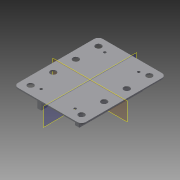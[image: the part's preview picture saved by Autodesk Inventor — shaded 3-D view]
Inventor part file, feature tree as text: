
AUTODESK INVENTOR PART (.ipt)
format: ipt  version: 2015 (Build 190159000, 159)  size: 258,048 bytes
history: native  units: mm
features: sketch x9, extrude x6, mirror x3, pattern_linear x3, fillet x2, plane x2, rib x2, hole x1
ambient origin geometry x8: Origin, YZ Plane, XZ Plane, XY Plane, X Axis, Y Axis, Z Axis, Center Point
bodies: Solid1 (feature_tree)
feature tree (28):
  extrude  "Extrusion1"  Depth=1.5mm
  fillet  "Fillet1"  Radius=1.5mm
  extrude  "Extrusion2"  Depth=5.0mm
  extrude  "Extrusion3"  Depth=80.0mm
  extrude  "Extrusion4"  Depth=1.5mm TaperAngle=0.0deg
  extrude  "Extrusion6"  Depth=80.0mm
  extrude  "Extrusion7"  Depth=35.0mm
  hole  "Hole1"  [1 undecoded]
  mirror  "Mirror3"
  mirror  "Mirror4"
  plane  "Work Plane1"
  rib  "Rib1"
  pattern_linear  "Rectangular Pattern1"  Spacing1=18.0mm  [1 undecoded]
  mirror  "Mirror5"
  plane  "Work Plane2"
  rib  "Rib2"
  pattern_linear  "Rectangular Pattern2"  Spacing1=2.5mm  [1 undecoded]
  fillet  "Fillet5"  Radius=2.5mm
  pattern_linear  "Rectangular Pattern3"  Spacing1=1.0mm  [1 undecoded]
  sketch  "Sketch1"  dims[d0=80.0mm d1=100.0mm d2=1.5mm d3=0.0mm]
  sketch  "Sketch2"  dims[d4=5.0mm d5=5.0mm]
  sketch  "Sketch3"  dims[d6=60.0mm d7=80.0mm]
  sketch  "Sketch4"  dims[d8=7.0mm d9=1.5mm d10=0.0mm]
  sketch  "Sketch6"  dims[d11=45.0mm d12=80.0mm]
  sketch  "Sketch7"  dims[d13=18.0mm d14=0.0mm d15=35.0mm]
  sketch  "Sketch8"  dims[d16=70.0mm d17=18.0mm d18=0.0mm]
  sketch  "Sketch9"  dims[d25=18.0mm d26=0.0mm]
  sketch  "Sketch10"  dims[d27=5.0mm d28=18.0mm d29=0.0mm d30=2.5mm d31=2.5mm d32=3.1mm d33=6.0mm d34=4.0mm d35=2.0mm d36=90.0deg d37=8.0mm d38=20.594885mm d39=1.0mm d40=2.0mm d41=0.0mm d42=0.0mm d43=1.0mm d44=1.0mm d45=30.0mm d47=30.0mm d48=1.0mm d49=2.0mm d50=0.0mm d51=0.0mm d52=1.0mm d53=1.0mm d54=50.0mm d56=10.0mm d57=0.5mm d58=40.0mm d60=80.0mm d61=20.0mm d63=60.0mm]
note: 4 required parameter values undecoded (feature->parameter linkage not recoverable at this tier; creation-order binding heuristic only, values carry confidence <= 0.55)
